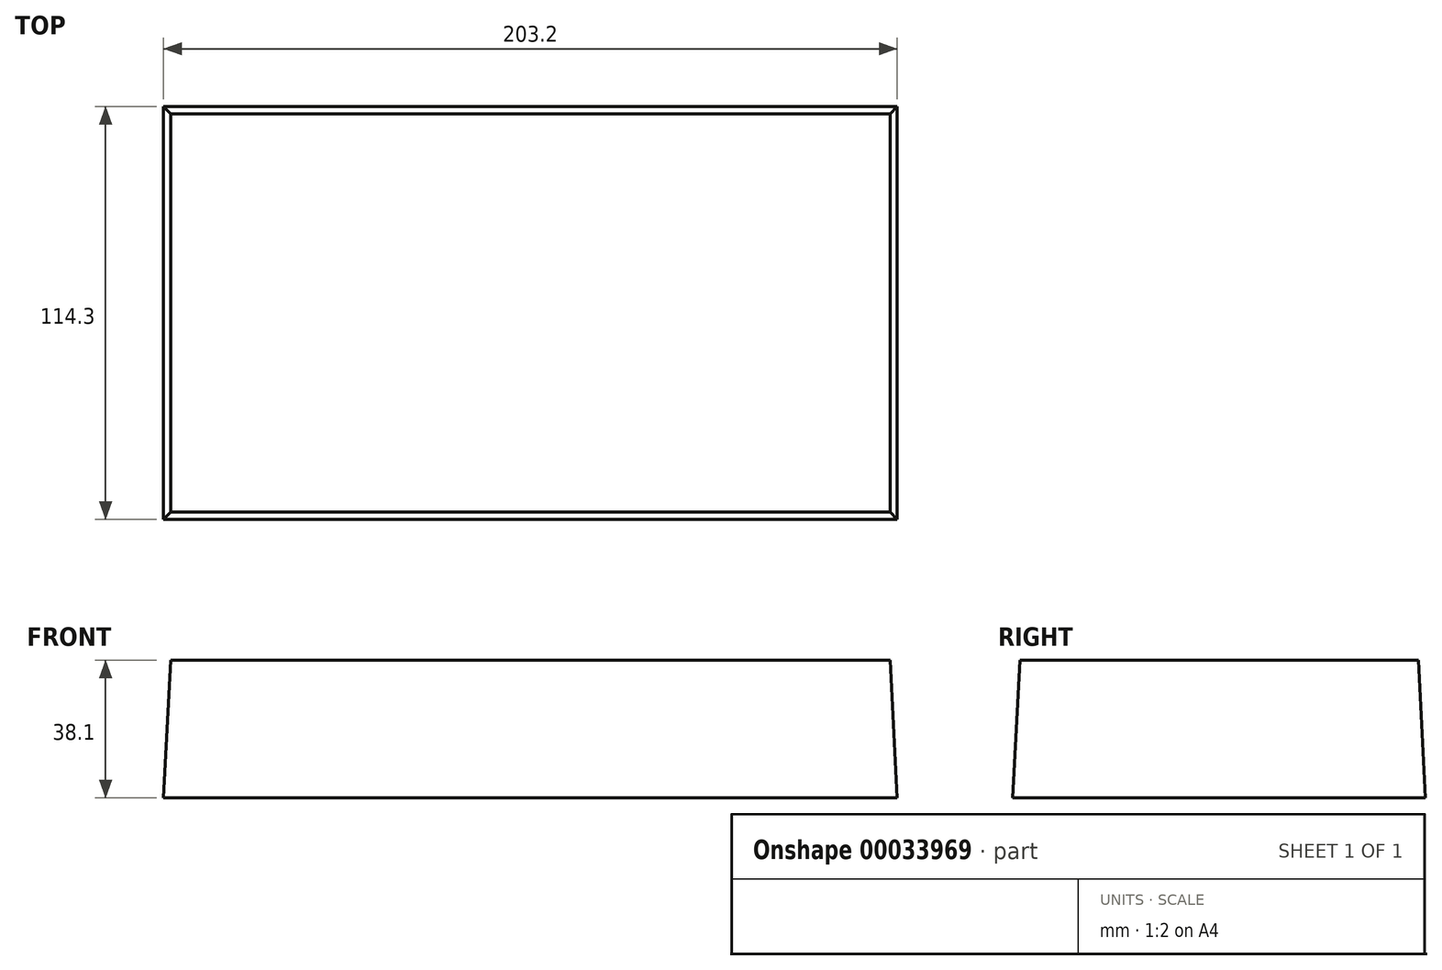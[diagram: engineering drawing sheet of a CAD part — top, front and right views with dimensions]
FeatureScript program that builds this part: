
annotation { "Feature Type Name" : "Feature", "Feature Type Description" : "" }
export const myFeature = defineFeature(function(context is Context, id is Id, definition is map)
    precondition{}
    {
        {
            var Q0;
            Q0=qCreatedBy(makeId("Top.planeOp"),FACE);
            var sketch = newSketch(context, id + "F0", { "sketchPlane" : qUnion([Q0])});
            skLineSegment(sketch, "E0.bottom", {"start": v(-132.8, 83.36) * mm, "end": v(70.4, 83.36) * mm});
            skLineSegment(sketch, "E0.top", {"start": v(-132.8, -30.94) * mm, "end": v(70.4, -30.94) * mm});
            skLineSegment(sketch, "E0.left", {"start": v(-132.8, 83.36) * mm, "end": v(-132.8, -30.94) * mm});
            skLineSegment(sketch, "E0.right", {"start": v(70.4, 83.36) * mm, "end": v(70.4, -30.94) * mm});
            skSolve(sketch);
        }
        {
            var Q0;
            Q0 = qSketchRegion(id + "F0", true);
            extrude(context, id + "F1", {"entities" : qUnion([Q0]), "depth" : 38.1 * mm, "hasDraft" : true, "draftAngle" : 3 * degree, "draftPullDirection" : true});
        }
    });
